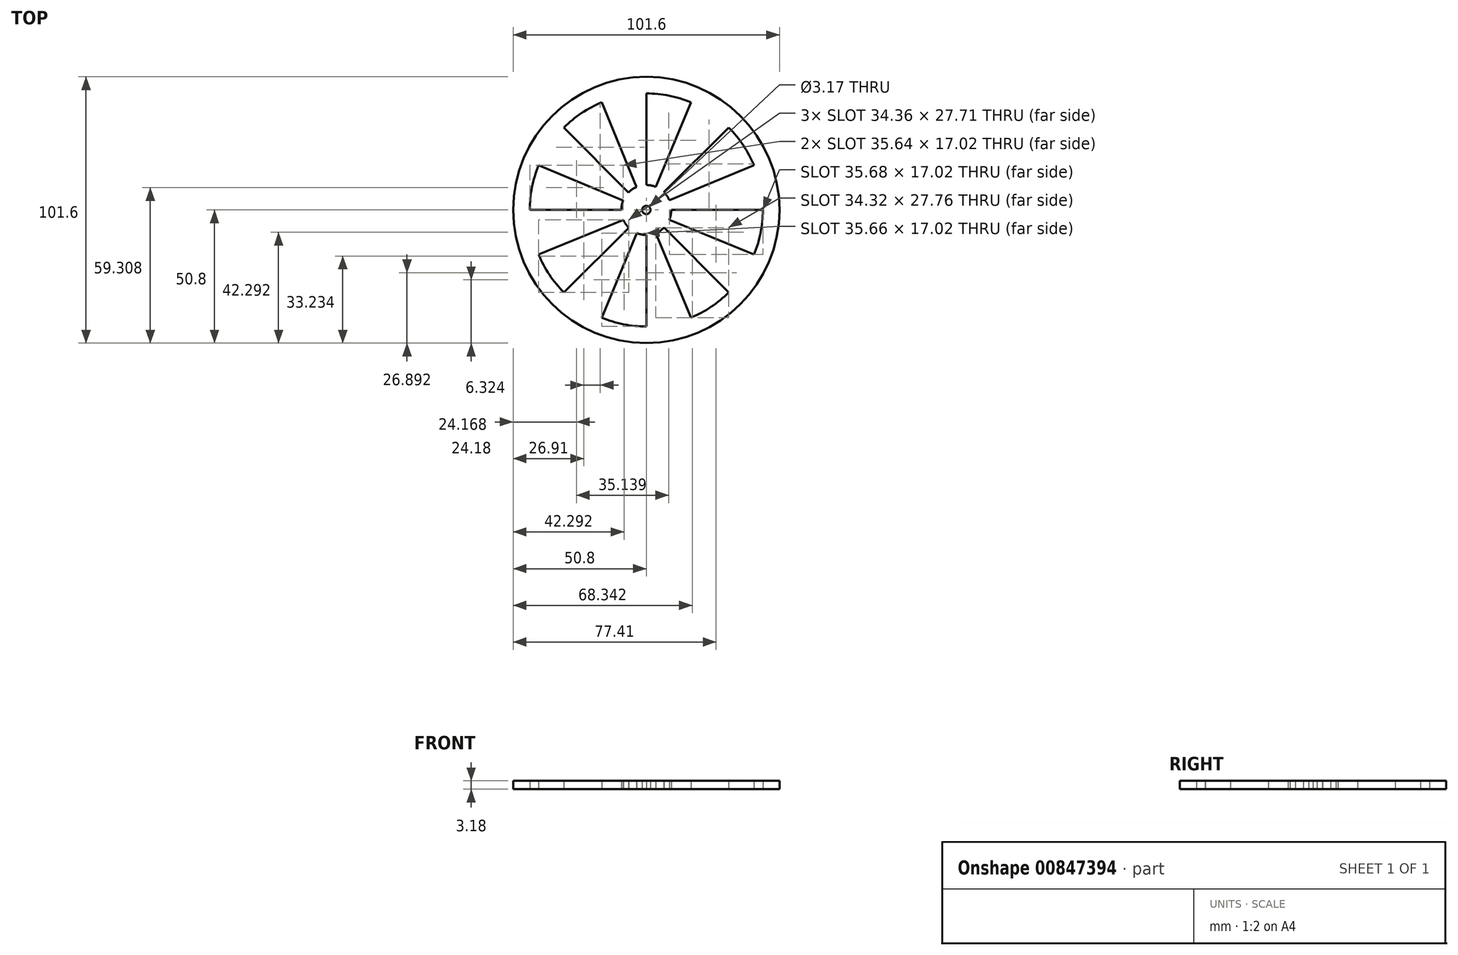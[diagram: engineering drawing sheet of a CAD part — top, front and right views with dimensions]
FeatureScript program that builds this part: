
annotation { "Feature Type Name" : "Feature", "Feature Type Description" : "" }
export const myFeature = defineFeature(function(context is Context, id is Id, definition is map)
    precondition{}
    {
        {
            var Q0;
            Q0=qCreatedBy(makeId("Top.planeOp"),FACE);
            var sketch = newSketch(context, id + "F0", { "sketchPlane" : qUnion([Q0])});
            skCircle(sketch, "E0", {"center": v(0, 0) * mm, "radius": 50.8 * mm});
            skArc(sketch, "E1", {"start": v(-31.42, 31.44) * mm, "mid": v(-41.06, 17.02) * mm, "end": v(-44.45, 0) * mm});
            skCircle(sketch, "E2", {"center": v(0, 0) * mm, "radius": 1.59 * mm});
            skCircle(sketch, "E3", {"center": v(0, 0) * mm, "radius": 9.53 * mm});
            skLineSegment(sketch, "E4", {"start": v(0, 9.52) * mm, "end": v(0, 44.45) * mm});
            skLineSegment(sketch, "E5", {"start": v(-9.52, 0) * mm, "end": v(-44.45, 0) * mm});
            skLineSegment(sketch, "E6", {"start": v(0, -9.52) * mm, "end": v(0, -44.45) * mm});
            skLineSegment(sketch, "E7", {"start": v(9.52, 0) * mm, "end": v(44.45, 0) * mm});
            skLineSegment(sketch, "E8", {"start": v(-31.42, 31.44) * mm, "end": v(-6.77, 6.7) * mm});
            skLineSegment(sketch, "E9", {"start": v(6.7, 6.77) * mm, "end": v(31.44, 31.42) * mm});
            skLineSegment(sketch, "E10", {"start": v(6.72, -6.75) * mm, "end": v(31.42, -31.44) * mm});
            skLineSegment(sketch, "E11", {"start": v(-6.71, -6.76) * mm, "end": v(-31.44, -31.42) * mm});
            skArc(sketch, "E12.trimOffspring", {"start": v(-31.44, -31.42) * mm, "mid": v(-17.02, -41.06) * mm, "end": v(0, -44.45) * mm});
            skArc(sketch, "E13.trimOffspring", {"start": v(31.42, -31.44) * mm, "mid": v(41.06, -17.02) * mm, "end": v(44.45, 0) * mm});
            skArc(sketch, "E14.trimOffspring", {"start": v(31.44, 31.42) * mm, "mid": v(17.02, 41.06) * mm, "end": v(0, 44.45) * mm});
            skArc(sketch, "E15", {"start": v(-31.42, 31.44) * mm, "mid": v(-17, 41.07) * mm, "end": v(0, 44.45) * mm});
            skArc(sketch, "E16", {"start": v(-44.45, 0) * mm, "mid": v(-41.07, -17) * mm, "end": v(-31.44, -31.42) * mm});
            skArc(sketch, "E17", {"start": v(31.42, -31.44) * mm, "mid": v(17, -41.07) * mm, "end": v(0, -44.45) * mm});
            skArc(sketch, "E18", {"start": v(31.44, 31.42) * mm, "mid": v(41.07, 17) * mm, "end": v(44.45, 0) * mm});
            skLineSegment(sketch, "E19", {"start": v(-41.06, 17.02) * mm, "end": v(-8.81, 3.61) * mm});
            skLineSegment(sketch, "E20", {"start": v(-17, 41.07) * mm, "end": v(-3.7, 8.77) * mm});
            skLineSegment(sketch, "E21", {"start": v(17.02, 41.06) * mm, "end": v(3.61, 8.81) * mm});
            skLineSegment(sketch, "E22", {"start": v(41.07, 17) * mm, "end": v(8.77, 3.72) * mm});
            skLineSegment(sketch, "E23", {"start": v(41.06, -17.02) * mm, "end": v(8.77, -3.72) * mm});
            skLineSegment(sketch, "E24", {"start": v(3.66, -8.8) * mm, "end": v(17, -41.07) * mm});
            skLineSegment(sketch, "E25", {"start": v(-17.02, -41.06) * mm, "end": v(-3.67, -8.8) * mm});
            skLineSegment(sketch, "E26", {"start": v(-41.07, -17) * mm, "end": v(-8.77, -3.7) * mm});
            skSolve(sketch);
        }
        {
            var Q0;
            Q0=makeQuery(id+"F0.imprint","IMPRINT",FACE,{"disambiguationData":[TD([[makeQuery(id+"F0.imprint","IMPRINT",EDGE,{"derivedFrom":sQuery(id+"F0.wireOp",EDGE,"E0")}),1.0]])]});
            var Q1;
            Q1=makeQuery(id+"F0.imprint","IMPRINT",FACE,{"disambiguationData":[TD([[makeQuery(id+"F0.imprint","IMPRINT",EDGE,{"derivedFrom":sQuery(id+"F0.wireOp",EDGE,"E2")}),-1.0]])]});
            var Q2;
            {var subQ0=sQuery(id+"F0.wireOp",EDGE,"E8");Q2=makeQuery(id+"F0.imprint","IMPRINT",FACE,{"disambiguationData":[TD([[makeQuery(id+"F0.imprint","IMPRINT",EDGE,{"derivedFrom":subQ0}),-1.0]])]});}
            var Q3;
            {var subQ0=sQuery(id+"F0.wireOp",EDGE,"E4");Q3=makeQuery(id+"F0.imprint","IMPRINT",FACE,{"disambiguationData":[TD([[makeQuery(id+"F0.imprint","IMPRINT",EDGE,{"derivedFrom":subQ0}),1.0]])]});}
            var Q4;
            {var subQ0=sQuery(id+"F0.wireOp",EDGE,"E9");Q4=makeQuery(id+"F0.imprint","IMPRINT",FACE,{"disambiguationData":[TD([[makeQuery(id+"F0.imprint","IMPRINT",EDGE,{"derivedFrom":subQ0}),1.0]])]});}
            var Q5;
            {var subQ0=sQuery(id+"F0.wireOp",EDGE,"E7");Q5=makeQuery(id+"F0.imprint","IMPRINT",FACE,{"disambiguationData":[TD([[makeQuery(id+"F0.imprint","IMPRINT",EDGE,{"derivedFrom":subQ0}),1.0]])]});}
            var Q6;
            {var subQ0=sQuery(id+"F0.wireOp",EDGE,"E10");Q6=makeQuery(id+"F0.imprint","IMPRINT",FACE,{"disambiguationData":[TD([[makeQuery(id+"F0.imprint","IMPRINT",EDGE,{"derivedFrom":subQ0}),1.0]])]});}
            var Q7;
            {var subQ0=sQuery(id+"F0.wireOp",EDGE,"E6");Q7=makeQuery(id+"F0.imprint","IMPRINT",FACE,{"disambiguationData":[TD([[makeQuery(id+"F0.imprint","IMPRINT",EDGE,{"derivedFrom":subQ0}),1.0]])]});}
            var Q8;
            {var subQ0=sQuery(id+"F0.wireOp",EDGE,"E11");Q8=makeQuery(id+"F0.imprint","IMPRINT",FACE,{"disambiguationData":[TD([[makeQuery(id+"F0.imprint","IMPRINT",EDGE,{"derivedFrom":subQ0}),1.0]])]});}
            var Q9;
            {var subQ0=sQuery(id+"F0.wireOp",EDGE,"E5");Q9=makeQuery(id+"F0.imprint","IMPRINT",FACE,{"disambiguationData":[TD([[makeQuery(id+"F0.imprint","IMPRINT",EDGE,{"derivedFrom":subQ0}),1.0]])]});}
            extrude(context, id + "F1", {"entities" : qUnion([Q0, Q1, Q2, Q3, Q4, Q5, Q6, Q7, Q8, Q9]), "depth" : 3.17 * mm, "offsetDistance" : 25.4 * mm});
        }
    });
